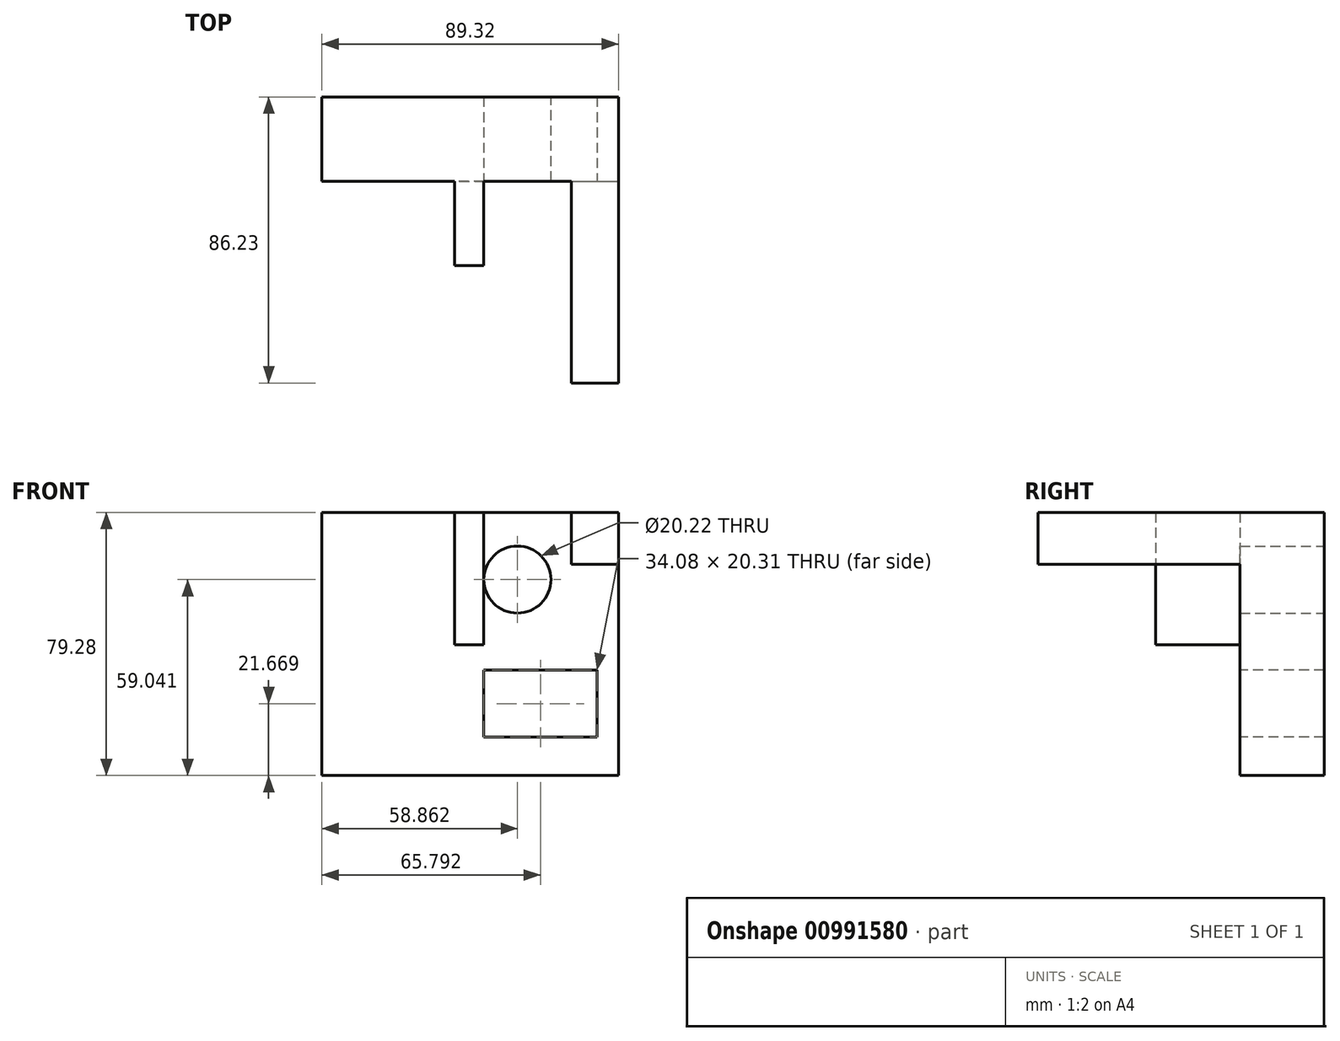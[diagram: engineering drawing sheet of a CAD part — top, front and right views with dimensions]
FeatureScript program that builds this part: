
annotation { "Feature Type Name" : "Feature", "Feature Type Description" : "" }
export const myFeature = defineFeature(function(context is Context, id is Id, definition is map)
    precondition{}
    {
        {
            var Q0;
            Q0=qCreatedBy(makeId("Front.planeOp"),FACE);
            var sketch = newSketch(context, id + "F0", { "sketchPlane" : qUnion([Q0])});
            skLineSegment(sketch, "E0.bottom", {"start": v(-39.9, 39.91) * mm, "end": v(49.42, 39.91) * mm});
            skLineSegment(sketch, "E0.top", {"start": v(-39.9, -39.37) * mm, "end": v(49.42, -39.37) * mm});
            skLineSegment(sketch, "E0.left", {"start": v(-39.9, 39.91) * mm, "end": v(-39.9, -39.37) * mm});
            skLineSegment(sketch, "E0.right", {"start": v(49.42, 39.91) * mm, "end": v(49.42, -39.37) * mm});
            skSolve(sketch);
        }
        {
            var Q0;
            Q0=makeQuery(id+"F0.imprint","IMPRINT",FACE,{"disambiguationData":[TD([[makeQuery(id+"F0.imprint","IMPRINT",EDGE,{"derivedFrom":sQuery(id+"F0.wireOp",EDGE,"E0.bottom")}),-1.0]])]});
            extrude(context, id + "F1", {"entities" : qUnion([Q0]), "depth" : 25.4 * mm, "offsetDistance" : 25.4 * mm});
        }
        {
            var Q0;
            Q0=makeQuery(id+"F1.opExtrude","CAP_FACE",FACE,{"disambiguationData":[OSD([sQuery(id+"F0.wireOp",EDGE,"E0.bottom"),sQuery(id+"F0.wireOp",EDGE,"E0.top"),sQuery(id+"F0.wireOp",EDGE,"E0.left"),sQuery(id+"F0.wireOp",EDGE,"E0.right")])],"isStart":false});
            var sketch = newSketch(context, id + "F2", { "sketchPlane" : qUnion([Q0])});
            skLineSegment(sketch, "E1.bottom", {"start": v(35.22, 39.91) * mm, "end": v(49.42, 39.91) * mm});
            skLineSegment(sketch, "E1.top", {"start": v(35.22, 24.27) * mm, "end": v(49.42, 24.27) * mm});
            skLineSegment(sketch, "E1.left", {"start": v(35.22, 39.91) * mm, "end": v(35.22, 24.27) * mm});
            skLineSegment(sketch, "E1.right", {"start": v(49.42, 39.91) * mm, "end": v(49.42, 24.27) * mm});
            skSolve(sketch);
        }
        {
            var Q0;
            Q0 = qSketchRegion(id + "F2", true);
            var Q1;
            Q1=makeQuery(id+"F2.imprint","IMPRINT",FACE,{"disambiguationData":[TD([[makeQuery(id+"F2.imprint","IMPRINT",EDGE,{"derivedFrom":sQuery(id+"F2.wireOp",EDGE,"E1.bottom")}),-1.0]])]});
            extrude(context, id + "F3", {"entities" : qUnion([Q0, Q1]), "operationType" : NewBodyOperationType.ADD, "depth" : 60.83 * mm, "offsetDistance" : 25.4 * mm});
        }
        {
            var Q0;
            Q0=makeQuery(id+"F1.opExtrude","CAP_FACE",FACE,{"disambiguationData":[OSD([sQuery(id+"F0.wireOp",EDGE,"E0.bottom"),sQuery(id+"F0.wireOp",EDGE,"E0.top"),sQuery(id+"F0.wireOp",EDGE,"E0.left"),sQuery(id+"F0.wireOp",EDGE,"E0.right")])],"isStart":false});
            var sketch = newSketch(context, id + "F4", { "sketchPlane" : qUnion([Q0])});
            skLineSegment(sketch, "E2.bottom", {"start": v(8.85, -7.55) * mm, "end": v(42.93, -7.55) * mm});
            skLineSegment(sketch, "E2.top", {"start": v(8.85, -27.86) * mm, "end": v(42.93, -27.86) * mm});
            skLineSegment(sketch, "E2.left", {"start": v(8.85, -7.55) * mm, "end": v(8.85, -27.86) * mm});
            skLineSegment(sketch, "E2.right", {"start": v(42.93, -7.55) * mm, "end": v(42.93, -27.86) * mm});
            skPoint(sketch, "E2.middle", {"position": v(25.9, -17.7) * mm});
            skPoint(sketch, "E2.cornerSnap0", {"position": v(49.42, -7.55) * mm});
            skSolve(sketch);
        }
        {
            var Q0;
            Q0 = qSketchRegion(id + "F4", true);
            var Q1;
            Q1=makeQuery(id+"F4.imprint","IMPRINT",FACE,{"disambiguationData":[TD([[makeQuery(id+"F4.imprint","IMPRINT",EDGE,{"derivedFrom":sQuery(id+"F4.wireOp",EDGE,"E2.bottom")}),-1.0]])]});
            extrude(context, id + "F5", {"entities" : qUnion([Q0, Q1]), "operationType" : NewBodyOperationType.REMOVE, "oppositeDirection" : true, "depth" : 25.4 * mm, "offsetDistance" : 25.4 * mm});
        }
        {
            var Q0;
            Q0=makeQuery(id+"F1.opExtrude","CAP_FACE",FACE,{"disambiguationData":[OSD([sQuery(id+"F0.wireOp",EDGE,"E0.bottom"),sQuery(id+"F0.wireOp",EDGE,"E0.top"),sQuery(id+"F0.wireOp",EDGE,"E0.left"),sQuery(id+"F0.wireOp",EDGE,"E0.right")])],"isStart":true});
            var sketch = newSketch(context, id + "F6", { "sketchPlane" : qUnion([Q0])});
            skCircle(sketch, "E3", {"center": v(-18.96, 19.67) * mm, "radius": 10.1 * mm});
            skSolve(sketch);
        }
        {
            var Q0;
            Q0=makeQuery(id+"F6.imprint","IMPRINT",FACE,{"disambiguationData":[TD([[makeQuery(id+"F6.imprint","IMPRINT",EDGE,{"derivedFrom":sQuery(id+"F6.wireOp",EDGE,"E3")}),1.0]])]});
            extrude(context, id + "F7", {"entities" : qUnion([Q0]), "operationType" : NewBodyOperationType.REMOVE, "oppositeDirection" : true, "depth" : 25.4 * mm, "offsetDistance" : 25.4 * mm});
        }
        {
            var Q0;
            Q0=makeQuery(id+"F1.opExtrude","CAP_FACE",FACE,{"disambiguationData":[OSD([sQuery(id+"F0.wireOp",EDGE,"E0.bottom"),sQuery(id+"F0.wireOp",EDGE,"E0.top"),sQuery(id+"F0.wireOp",EDGE,"E0.left"),sQuery(id+"F0.wireOp",EDGE,"E0.right")])],"isStart":false});
            var sketch = newSketch(context, id + "F8", { "sketchPlane" : qUnion([Q0])});
            skLineSegment(sketch, "E4.bottom", {"start": v(8.85, 39.91) * mm, "end": v(0, 39.91) * mm});
            skLineSegment(sketch, "E4.top", {"start": v(8.85, 0) * mm, "end": v(0, 0) * mm});
            skLineSegment(sketch, "E4.left", {"start": v(8.85, 39.91) * mm, "end": v(8.85, 0) * mm});
            skLineSegment(sketch, "E4.right", {"start": v(0, 39.91) * mm, "end": v(0, 0) * mm});
            skSolve(sketch);
        }
        {
            var Q0;
            Q0=makeQuery(id+"F8.imprint","IMPRINT",FACE,{"disambiguationData":[TD([[makeQuery(id+"F8.imprint","IMPRINT",EDGE,{"derivedFrom":makeQuery(id+"F7.boolean.opBoolean","COPY",EDGE,{"derivedFrom":makeQuery(id+"F7.opExtrude","CAP_EDGE",EDGE,{"disambiguationData":[OSD([sQuery(id+"F6.wireOp",EDGE,"E3")])],"isStart":false})})}),-1.0]])]});
            var Q1;
            {var subQ3=sQuery(id+"F8.wireOp",EDGE,"E4.bottom");Q1=makeQuery(id+"F8.imprint","IMPRINT",FACE,{"disambiguationData":[TD([[makeQuery(id+"F8.imprint","IMPRINT",EDGE,{"derivedFrom":subQ3}),-1.0]])]});}
            var Q2;
            Q2 = qBodyType(qCreatedBy(id + "F8" ,EDGE), BodyType.WIRE);
            var Q3;
            Q3=sQuery(id+"F8.wireOp",EDGE,"E4.right");
            var Q4;
            Q4=sQuery(id+"F8.wireOp",EDGE,"E4.left");
            extrude(context, id + "F9", {"entities" : qUnion([Q0, Q1]), "operationType" : NewBodyOperationType.ADD, "surfaceEntities" : qUnion([Q2, Q3, Q4]), "depth" : 25.4 * mm, "offsetDistance" : 25.4 * mm});
        }
    });
